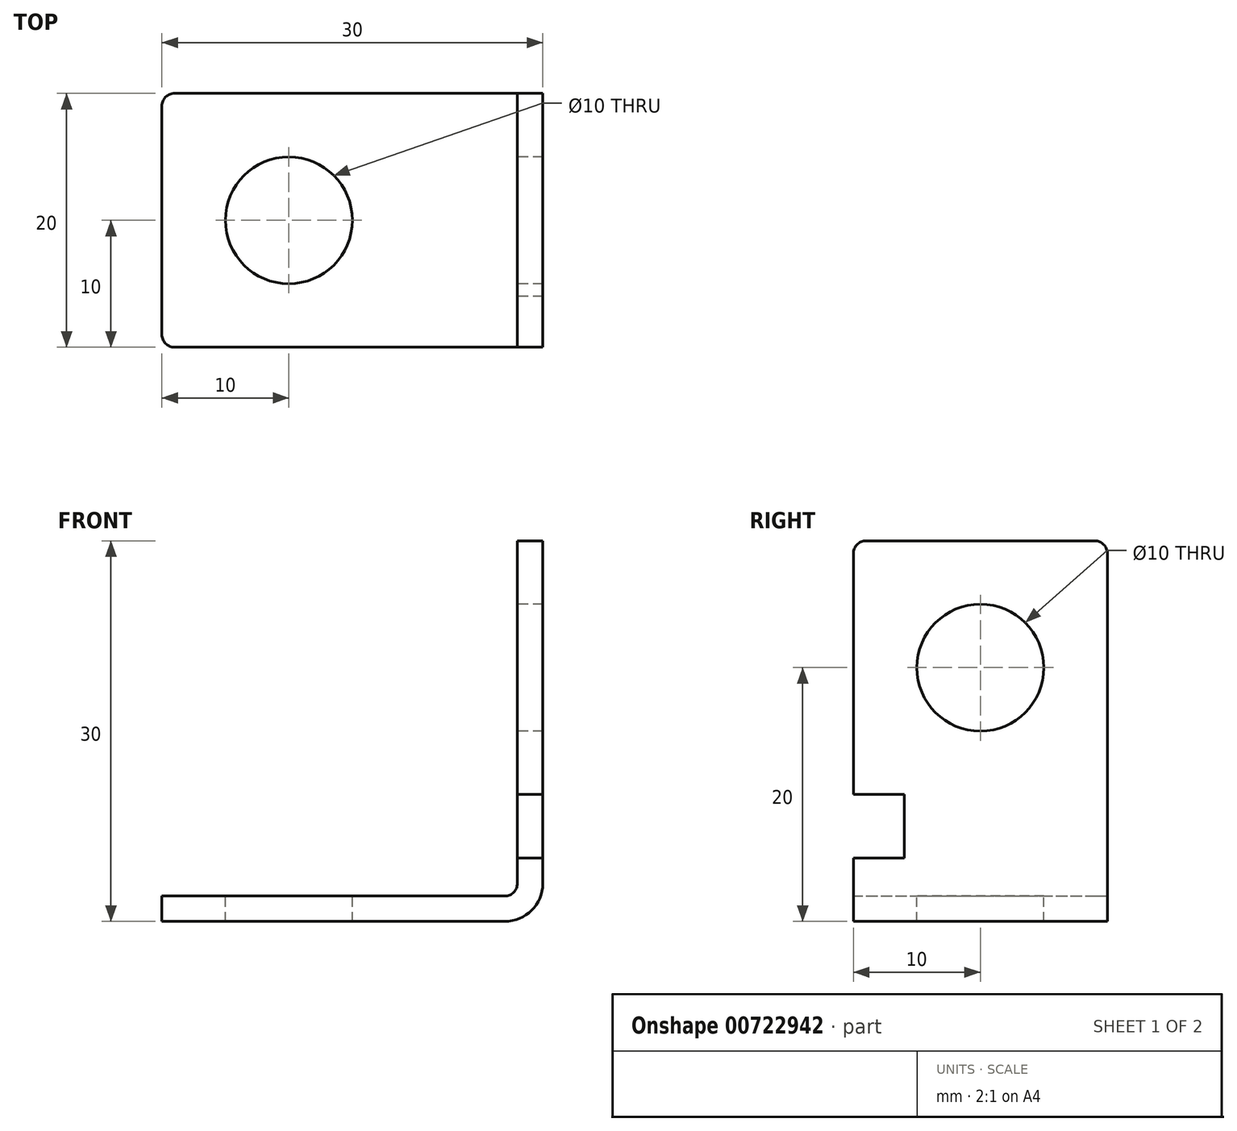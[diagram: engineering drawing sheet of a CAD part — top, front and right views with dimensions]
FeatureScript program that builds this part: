
annotation { "Feature Type Name" : "Feature", "Feature Type Description" : "" }
export const myFeature = defineFeature(function(context is Context, id is Id, definition is map)
    precondition{}
    {
        {
            var Q0;
            Q0=qCreatedBy(makeId("Front.planeOp"),FACE);
            var sketch = newSketch(context, id + "F0", { "sketchPlane" : qUnion([Q0])});
            skLineSegment(sketch, "E0", {"start": v(0, 0) * mm, "end": v(30, 0) * mm});
            skLineSegment(sketch, "E1", {"start": v(30, 0) * mm, "end": v(30, 30) * mm});
            skLineSegment(sketch, "E2", {"start": v(30, 30) * mm, "end": v(28, 30) * mm});
            skLineSegment(sketch, "E3", {"start": v(28, 30) * mm, "end": v(28, 2) * mm});
            skLineSegment(sketch, "E4", {"start": v(28, 2) * mm, "end": v(0, 2) * mm});
            skLineSegment(sketch, "E5", {"start": v(0, 2) * mm, "end": v(0, 0) * mm});
            skSolve(sketch);
        }
        {
            var Q0;
            Q0 = qSketchRegion(id + "F0", true);
            extrude(context, id + "F1", {"entities" : qUnion([Q0]), "depth" : 20 * mm, "offsetDistance" : 25 * mm});
        }
        {
            var Q0;
            Q0=makeQuery(id+"F1.opExtrude","SWEPT_FACE",FACE,{"disambiguationData":[OSD([sQuery(id+"F0.wireOp",EDGE,"E4")])]});
            var sketch = newSketch(context, id + "F2", { "sketchPlane" : qUnion([Q0])});
            skCircle(sketch, "E6", {"center": v(10, -10) * mm, "radius": 5 * mm});
            skLineSegment(sketch, "E7", {"start": v(0, -10) * mm, "end": v(28, -10) * mm, "construction": true});
            skSolve(sketch);
        }
        {
            var Q0;
            Q0 = qSketchRegion(id + "F2", true);
            extrude(context, id + "F3", {"entities" : qUnion([Q0]), "operationType" : NewBodyOperationType.REMOVE, "endBound" : BoundingType.THROUGH_ALL, "oppositeDirection" : true, "depth" : 25 * mm, "offsetDistance" : 25 * mm});
        }
        {
            var Q0;
            Q0=makeQuery(id+"F1.opExtrude","SWEPT_FACE",FACE,{"disambiguationData":[OSD([sQuery(id+"F0.wireOp",EDGE,"E3")])]});
            var sketch = newSketch(context, id + "F4", { "sketchPlane" : qUnion([Q0])});
            skLineSegment(sketch, "E8", {"start": v(10, 30) * mm, "end": v(10, 2) * mm, "construction": true});
            skCircle(sketch, "E9", {"center": v(10, 20) * mm, "radius": 5 * mm});
            skSolve(sketch);
        }
        {
            var Q0;
            Q0 = qSketchRegion(id + "F4", true);
            extrude(context, id + "F5", {"entities" : qUnion([Q0]), "operationType" : NewBodyOperationType.REMOVE, "endBound" : BoundingType.THROUGH_ALL, "oppositeDirection" : true, "depth" : 25 * mm, "offsetDistance" : 25 * mm});
        }
        {
            var Q0;
            Q0=makeQuery(id+"F1.opExtrude","SWEPT_FACE",FACE,{"disambiguationData":[OSD([sQuery(id+"F0.wireOp",EDGE,"E3")])]});
            var sketch = newSketch(context, id + "F6", { "sketchPlane" : qUnion([Q0])});
            skLineSegment(sketch, "E10", {"start": v(20, 10) * mm, "end": v(16, 10) * mm});
            skLineSegment(sketch, "E11", {"start": v(16, 10) * mm, "end": v(16, 5) * mm});
            skLineSegment(sketch, "E12", {"start": v(16, 5) * mm, "end": v(20, 5) * mm});
            skLineSegment(sketch, "E13", {"start": v(20, 10) * mm, "end": v(20, 5) * mm});
            skSolve(sketch);
        }
        {
            var Q0;
            Q0 = qSketchRegion(id + "F6", true);
            extrude(context, id + "F7", {"entities" : qUnion([Q0]), "operationType" : NewBodyOperationType.REMOVE, "endBound" : BoundingType.THROUGH_ALL, "oppositeDirection" : true, "depth" : 25 * mm, "offsetDistance" : 25 * mm});
        }
        {
            var Q0;
            Q0=makeQuery(id+"F1.opExtrude","CAP_EDGE",EDGE,{"disambiguationData":[OSD([sQuery(id+"F0.wireOp",EDGE,"E2")])],"isStart":true});
            var Q1;
            Q1=makeQuery(id+"F1.opExtrude","CAP_EDGE",EDGE,{"disambiguationData":[OSD([sQuery(id+"F0.wireOp",EDGE,"E2")])],"isStart":false});
            var Q2;
            Q2=makeQuery(id+"F1.opExtrude","CAP_EDGE",EDGE,{"disambiguationData":[OSD([sQuery(id+"F0.wireOp",EDGE,"E5")])],"isStart":false});
            var Q3;
            Q3=makeQuery(id+"F1.opExtrude","CAP_EDGE",EDGE,{"disambiguationData":[OSD([sQuery(id+"F0.wireOp",EDGE,"E5")])],"isStart":true});
            fillet(context, id + "F8", {"entities" : qUnion([Q0, Q1, Q2, Q3]), "radius" : 1 * mm, "tangentPropagation" : true, "allowEdgeOverflow" : false});
        }
        {
            var Q0;
            Q0=makeQuery(id+"F1.opExtrude","SWEPT_EDGE",EDGE,{"disambiguationData":[OSD([sQuery(id+"F0.wireOp",EDGE,"E3"),sQuery(id+"F0.wireOp",EDGE,"E4")])]});
            fillet(context, id + "F9", {"entities" : qUnion([Q0]), "radius" : 1 * mm, "tangentPropagation" : true, "allowEdgeOverflow" : false});
        }
        {
            var Q0;
            Q0=makeQuery(id+"F1.opExtrude","SWEPT_EDGE",EDGE,{"disambiguationData":[OSD([sQuery(id+"F0.wireOp",EDGE,"E0"),sQuery(id+"F0.wireOp",EDGE,"E1")])]});
            fillet(context, id + "F10", {"entities" : qUnion([Q0]), "radius" : 3 * mm, "tangentPropagation" : true, "allowEdgeOverflow" : false});
        }
    });
